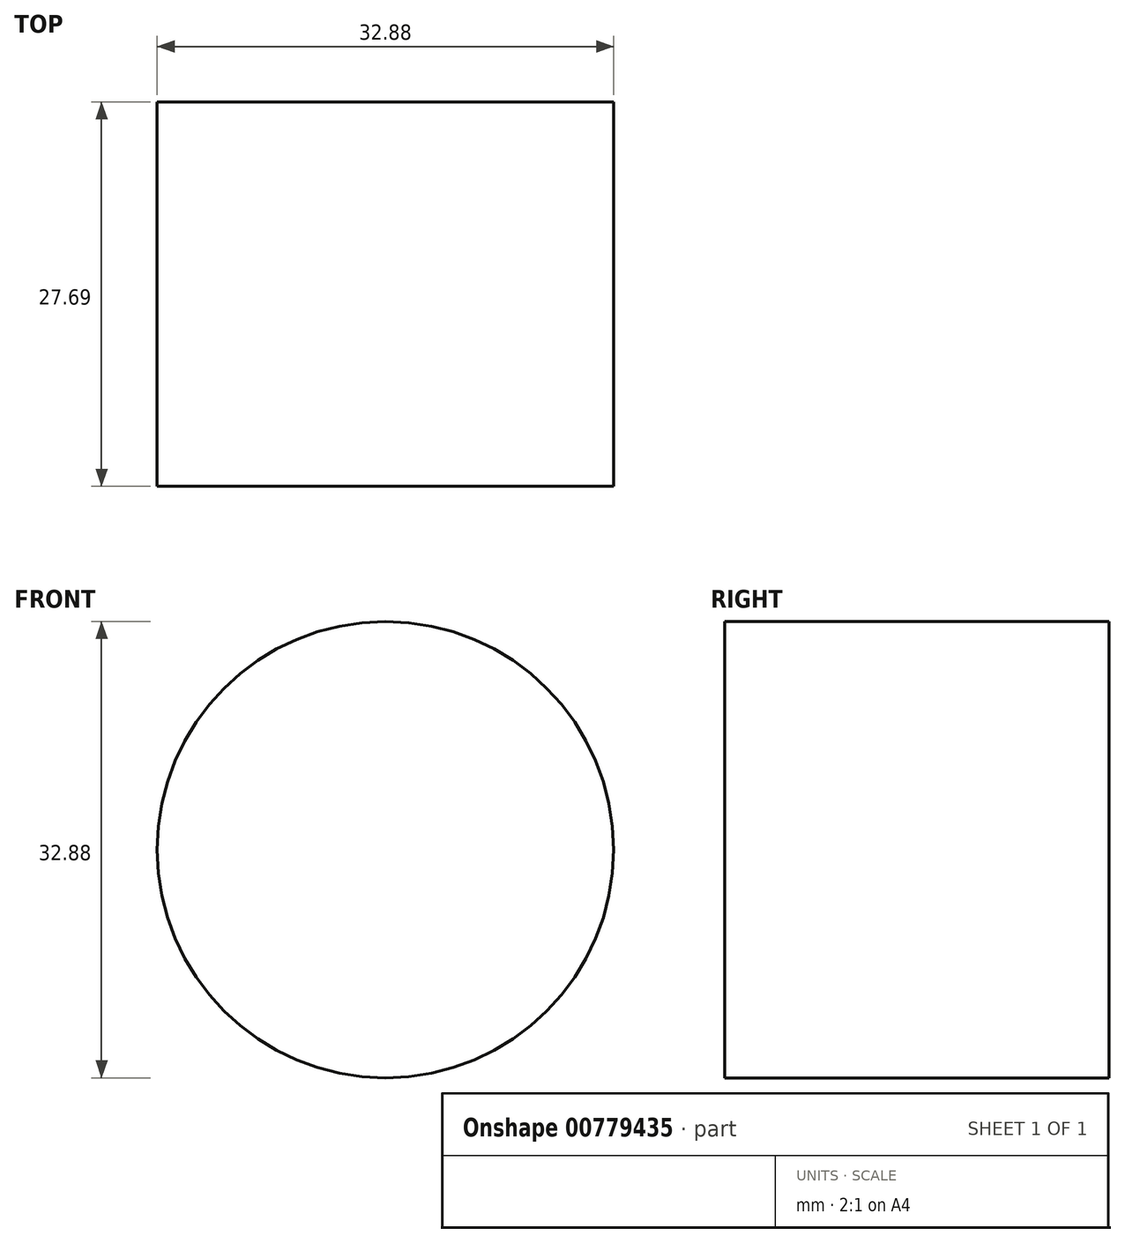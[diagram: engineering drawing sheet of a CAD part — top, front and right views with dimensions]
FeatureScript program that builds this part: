
annotation { "Feature Type Name" : "Feature", "Feature Type Description" : "" }
export const myFeature = defineFeature(function(context is Context, id is Id, definition is map)
    precondition{}
    {
        {
            var Q0;
            Q0=qCreatedBy(makeId("Front.planeOp"),FACE);
            var sketch = newSketch(context, id + "F0", { "sketchPlane" : qUnion([Q0])});
            skCircle(sketch, "E0", {"center": v(0, -7.2) * mm, "radius": 16.44 * mm});
            skSolve(sketch);
        }
        {
            var Q0;
            Q0 = qSketchRegion(id + "F0", true);
            extrude(context, id + "F1", {"entities" : qUnion([Q0]), "depth" : 27.7 * mm, "offsetDistance" : 25.4 * mm});
        }
    });
